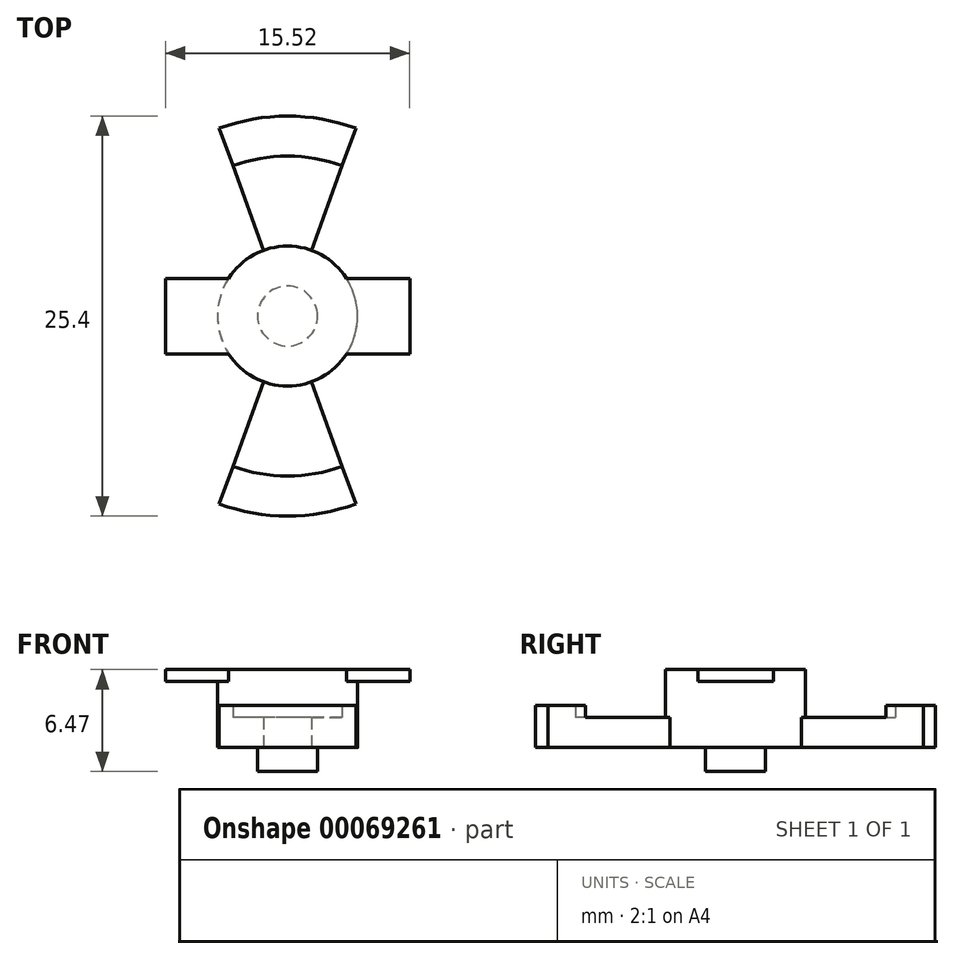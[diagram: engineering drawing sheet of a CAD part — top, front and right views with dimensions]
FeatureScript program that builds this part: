
annotation { "Feature Type Name" : "Feature", "Feature Type Description" : "" }
export const myFeature = defineFeature(function(context is Context, id is Id, definition is map)
    precondition{}
    {
        {
            var Q0;
            Q0=qCreatedBy(makeId("Top.planeOp"),FACE);
            var sketch = newSketch(context, id + "F0", { "sketchPlane" : qUnion([Q0])});
            skCircle(sketch, "E0", {"center": v(0, 0) * mm, "radius": 4.45 * mm});
            skCircle(sketch, "E1", {"center": v(0, 0) * mm, "radius": 12.7 * mm});
            skCircle(sketch, "E2", {"center": v(0, 0) * mm, "radius": 10.16 * mm});
            skLineSegment(sketch, "E3", {"start": v(-1.52, 4.18) * mm, "end": v(-4.34, 11.93) * mm});
            skLineSegment(sketch, "E4", {"start": v(0, 0) * mm, "end": v(-12.7, 0) * mm});
            skLineSegment(sketch, "E5", {"start": v(0, 0) * mm, "end": v(0, 12.7) * mm});
            skLineSegment(sketch, "E6.MirrorCS", {"start": v(1.52, 4.18) * mm, "end": v(4.34, 11.93) * mm});
            skLineSegment(sketch, "E7.MirrorCS", {"start": v(-1.52, -4.18) * mm, "end": v(-4.34, -11.93) * mm});
            skLineSegment(sketch, "E8.MirrorCS", {"start": v(1.52, -4.18) * mm, "end": v(4.34, -11.93) * mm});
            skLineSegment(sketch, "E9", {"start": v(-1.52, 4.18) * mm, "end": v(0, 0) * mm});
            skSolve(sketch);
        }
        {
            var Q0;
            {var subQ0=sQuery(id+"F0.wireOp",EDGE,"E5");var subQ1=sQuery(id+"F0.wireOp",EDGE,"E1");var subQ2=makeQuery(id+"F0.imprint","INTERSECT",VERTEX,{"derivedFrom":[subQ1,subQ0]});Q0=makeQuery(id+"F0.imprint","IMPRINT",FACE,{"disambiguationData":[TD([[makeQuery(id+"F0.imprint","IMPRINT",EDGE,{"disambiguationData":[TD([[subQ2,1.0]])],"derivedFrom":subQ1}),1.0]])]});}
            var Q1;
            {var subQ0=sQuery(id+"F0.wireOp",EDGE,"E3");var subQ1=sQuery(id+"F0.wireOp",EDGE,"E1");var subQ2=makeQuery(id+"F0.imprint","INTERSECT",VERTEX,{"derivedFrom":[subQ1,subQ0]});Q1=makeQuery(id+"F0.imprint","IMPRINT",FACE,{"disambiguationData":[TD([[makeQuery(id+"F0.imprint","IMPRINT",EDGE,{"disambiguationData":[TD([[subQ2,1.0]])],"derivedFrom":subQ1}),1.0]])]});}
            var Q2;
            {var subQ0=sQuery(id+"F0.wireOp",EDGE,"E7.MirrorCS");var subQ1=sQuery(id+"F0.wireOp",EDGE,"E1");var subQ2=makeQuery(id+"F0.imprint","INTERSECT",VERTEX,{"derivedFrom":[subQ1,subQ0]});Q2=makeQuery(id+"F0.imprint","IMPRINT",FACE,{"disambiguationData":[TD([[makeQuery(id+"F0.imprint","IMPRINT",EDGE,{"disambiguationData":[TD([[subQ2,-1.0]])],"derivedFrom":subQ1}),1.0]])]});}
            var Q3;
            {var subQ0=sQuery(id+"F0.wireOp",EDGE,"E9");Q3=makeQuery(id+"F0.imprint","IMPRINT",FACE,{"disambiguationData":[TD([[makeQuery(id+"F0.imprint","IMPRINT",EDGE,{"derivedFrom":subQ0}),-1.0]])]});}
            var Q4;
            {var subQ0=sQuery(id+"F0.wireOp",EDGE,"E0");var subQ1=makeQuery(id+"F0.imprint","INTERSECT",VERTEX,{"derivedFrom":[subQ0,sQuery(id+"F0.wireOp",EDGE,"E6.MirrorCS")]});Q4=makeQuery(id+"F0.imprint","IMPRINT",FACE,{"disambiguationData":[TD([[makeQuery(id+"F0.imprint","IMPRINT",EDGE,{"disambiguationData":[TD([[subQ1,-1.0]])],"derivedFrom":subQ0}),1.0]])]});}
            var Q5;
            {var subQ0=sQuery(id+"F0.wireOp",EDGE,"E7.MirrorCS");var subQ1=sQuery(id+"F0.wireOp",EDGE,"E0");var subQ2=makeQuery(id+"F0.imprint","INTERSECT",VERTEX,{"derivedFrom":[subQ1,subQ0]});Q5=makeQuery(id+"F0.imprint","IMPRINT",FACE,{"disambiguationData":[TD([[makeQuery(id+"F0.imprint","IMPRINT",EDGE,{"disambiguationData":[TD([[subQ2,-1.0]])],"derivedFrom":subQ1}),-1.0]])]});}
            var Q6;
            {var subQ0=sQuery(id+"F0.wireOp",EDGE,"E9");Q6=makeQuery(id+"F0.imprint","IMPRINT",FACE,{"disambiguationData":[TD([[makeQuery(id+"F0.imprint","IMPRINT",EDGE,{"derivedFrom":subQ0}),1.0]])]});}
            var Q7;
            {var subQ3=sQuery(id+"F0.wireOp",EDGE,"E5");var subQ5=sQuery(id+"F0.wireOp",EDGE,"E2");var subQ7=makeQuery(id+"F0.imprint","INTERSECT",VERTEX,{"derivedFrom":[subQ5,subQ3]});Q7=makeQuery(id+"F0.imprint","IMPRINT",FACE,{"disambiguationData":[TD([[makeQuery(id+"F0.imprint","IMPRINT",EDGE,{"disambiguationData":[TD([[subQ7,-1.0]])],"derivedFrom":subQ5}),1.0]])]});}
            var Q8;
            {var subQ0=sQuery(id+"F0.wireOp",EDGE,"E6.MirrorCS");var subQ1=sQuery(id+"F0.wireOp",EDGE,"E0");var subQ2=makeQuery(id+"F0.imprint","INTERSECT",VERTEX,{"derivedFrom":[subQ1,subQ0]});Q8=makeQuery(id+"F0.imprint","IMPRINT",FACE,{"disambiguationData":[TD([[makeQuery(id+"F0.imprint","IMPRINT",EDGE,{"disambiguationData":[TD([[subQ2,-1.0]])],"derivedFrom":subQ1}),-1.0]])]});}
            extrude(context, id + "F1", {"entities" : qUnion([Q0, Q1, Q2, Q3, Q4, Q5, Q6, Q7, Q8]), "depth" : 1.9 * mm});
        }
        {
            var Q0;
            Q0=makeQuery(id+"F1.opExtrude","CAP_FACE",FACE,{"disambiguationData":[OSD([sQuery(id+"F0.wireOp",EDGE,"E0"),sQuery(id+"F0.wireOp",EDGE,"E1"),sQuery(id+"F0.wireOp",EDGE,"E3"),sQuery(id+"F0.wireOp",EDGE,"E6.MirrorCS"),sQuery(id+"F0.wireOp",EDGE,"E7.MirrorCS"),sQuery(id+"F0.wireOp",EDGE,"E8.MirrorCS")])],"isStart":false});
            var sketch = newSketch(context, id + "F2", { "sketchPlane" : qUnion([Q0])});
            skCircle(sketch, "E10", {"center": v(0, 0) * mm, "radius": 12.7 * mm});
            skCircle(sketch, "E11", {"center": v(0, 0) * mm, "radius": 10.16 * mm});
            skLineSegment(sketch, "E12", {"start": v(4.34, -11.93) * mm, "end": v(3.47, -9.55) * mm});
            skLineSegment(sketch, "E13", {"start": v(-4.34, -11.93) * mm, "end": v(-3.47, -9.55) * mm});
            skLineSegment(sketch, "E14", {"start": v(-4.34, 11.93) * mm, "end": v(-3.47, 9.55) * mm});
            skLineSegment(sketch, "E15", {"start": v(4.34, 11.93) * mm, "end": v(3.47, 9.55) * mm});
            skSolve(sketch);
        }
        {
            var Q0;
            {var subQ0=sQuery(id+"F2.wireOp",EDGE,"E14");Q0=makeQuery(id+"F2.imprint","IMPRINT",FACE,{"disambiguationData":[TD([[makeQuery(id+"F2.imprint","IMPRINT",EDGE,{"derivedFrom":subQ0}),-1.0]])]});}
            var Q1;
            {var subQ2=sQuery(id+"F2.wireOp",EDGE,"E12");Q1=makeQuery(id+"F2.imprint","IMPRINT",FACE,{"disambiguationData":[TD([[makeQuery(id+"F2.imprint","IMPRINT",EDGE,{"derivedFrom":subQ2}),-1.0]])]});}
            extrude(context, id + "F3", {"entities" : qUnion([Q0, Q1]), "operationType" : NewBodyOperationType.ADD, "depth" : 0.76 * mm});
        }
        {
            var Q0;
            Q0=makeQuery(id+"F1.opExtrude","CAP_FACE",FACE,{"disambiguationData":[OSD([sQuery(id+"F0.wireOp",EDGE,"E0"),sQuery(id+"F0.wireOp",EDGE,"E1"),sQuery(id+"F0.wireOp",EDGE,"E3"),sQuery(id+"F0.wireOp",EDGE,"E6.MirrorCS"),sQuery(id+"F0.wireOp",EDGE,"E7.MirrorCS"),sQuery(id+"F0.wireOp",EDGE,"E8.MirrorCS")])],"isStart":false});
            var sketch = newSketch(context, id + "F4", { "sketchPlane" : qUnion([Q0])});
            skCircle(sketch, "E16", {"center": v(0, 0) * mm, "radius": 4.45 * mm});
            skSolve(sketch);
        }
        {
            var Q0;
            Q0 = qSketchRegion(id + "F4", true);
            extrude(context, id + "F5", {"entities" : qUnion([Q0]), "operationType" : NewBodyOperationType.ADD, "depth" : 3.05 * mm});
        }
        {
            var Q0;
            Q0=makeQuery(id+"F5.opExtrude","CAP_FACE",FACE,{"disambiguationData":[OSD([sQuery(id+"F4.wireOp",EDGE,"E16")])],"isStart":false});
            var sketch = newSketch(context, id + "F6", { "sketchPlane" : qUnion([Q0])});
            skLineSegment(sketch, "E17.rect.bottom", {"start": v(-7.76, 2.4) * mm, "end": v(7.76, 2.4) * mm});
            skLineSegment(sketch, "E17.rect.top", {"start": v(-7.76, -2.4) * mm, "end": v(7.76, -2.4) * mm});
            skLineSegment(sketch, "E17.rect.left", {"start": v(-7.76, 2.4) * mm, "end": v(-7.76, -2.4) * mm});
            skLineSegment(sketch, "E17.rect.right", {"start": v(7.76, 2.4) * mm, "end": v(7.76, -2.4) * mm});
            skPoint(sketch, "E17.rect.middle", {"position": v(0, 0) * mm});
            skSolve(sketch);
        }
        {
            var Q0;
            Q0 = qSketchRegion(id + "F6", true);
            extrude(context, id + "F7", {"entities" : qUnion([Q0]), "operationType" : NewBodyOperationType.ADD, "oppositeDirection" : true, "depth" : 0.76 * mm});
        }
        {
            var Q0;
            Q0=makeQuery(id+"F1.opExtrude","CAP_FACE",FACE,{"disambiguationData":[OSD([sQuery(id+"F0.wireOp",EDGE,"E0"),sQuery(id+"F0.wireOp",EDGE,"E1"),sQuery(id+"F0.wireOp",EDGE,"E3"),sQuery(id+"F0.wireOp",EDGE,"E6.MirrorCS"),sQuery(id+"F0.wireOp",EDGE,"E7.MirrorCS"),sQuery(id+"F0.wireOp",EDGE,"E8.MirrorCS")])],"isStart":true});
            var sketch = newSketch(context, id + "F8", { "sketchPlane" : qUnion([Q0])});
            skCircle(sketch, "E18", {"center": v(0, 0) * mm, "radius": 1.9 * mm});
            skSolve(sketch);
        }
        {
            var Q0;
            Q0 = qSketchRegion(id + "F8", true);
            extrude(context, id + "F9", {"entities" : qUnion([Q0]), "operationType" : NewBodyOperationType.ADD, "depth" : 1.52 * mm});
        }
    });
